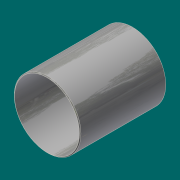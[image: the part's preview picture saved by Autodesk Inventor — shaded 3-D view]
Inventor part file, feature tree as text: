
AUTODESK INVENTOR PART (.ipt)
format: ipt  version: 2017.3 (Build 213256000, 256)  size: 102,912 bytes
history: native  units: in
note: dims shown in document units (in); Inventor stores cm internally (conversion verified against a paired STEP export)
features: chamfer x2, extrude x1, sketch x1
ambient origin geometry x8: Origin, YZ Plane, XZ Plane, XY Plane, X Axis, Y Axis, Z Axis, Center Point
bodies: Solid1 (feature_tree)
feature tree (4):
  extrude  "Extrusion1"  Depth=43.9218in
  chamfer  "Chamfer1"  Distance=43.9218in
  chamfer  "Chamfer2"  Distance=0.4375in
  sketch  "Sketch1"  dims[d0=34.0in d1=33.0in d2=43.9218in d3=0.0in d4=0.4375in d5=0.125in d6=0.2577in d7=0.4375in d8=0.125in d9=0.2577in]
